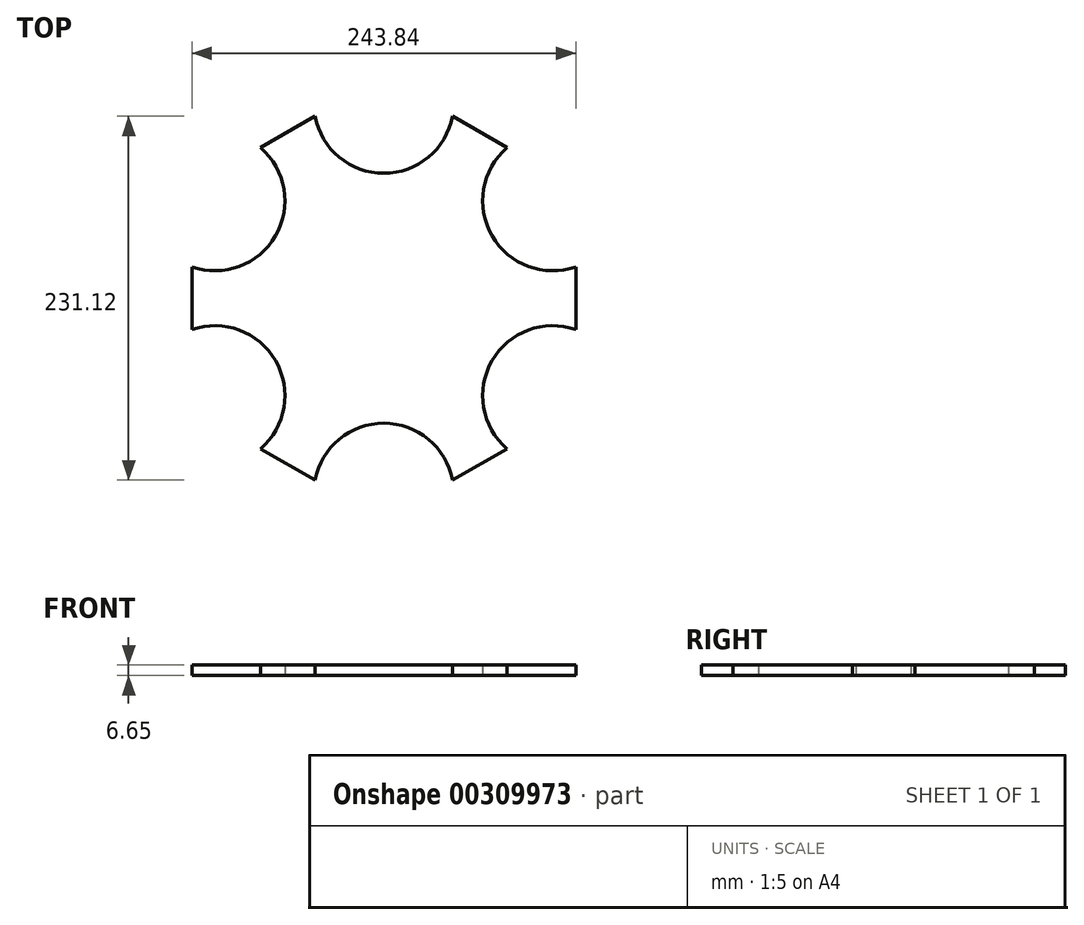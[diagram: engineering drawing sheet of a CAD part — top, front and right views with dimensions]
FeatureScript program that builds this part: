
annotation { "Feature Type Name" : "Feature", "Feature Type Description" : "" }
export const myFeature = defineFeature(function(context is Context, id is Id, definition is map)
    precondition{}
    {
        {
            var Q0;
            Q0=qCreatedBy(makeId("Top.planeOp"),FACE);
            var sketch = newSketch(context, id + "F0", { "sketchPlane" : qUnion([Q0])});
            skArc(sketch, "E0", {"start": v(-43.68, 115.56) * mm, "mid": v(0, 79.38) * mm, "end": v(43.68, 115.56) * mm});
            skArc(sketch, "E1.1.0", {"start": v(-121.92, 19.96) * mm, "mid": v(-68.74, 39.69) * mm, "end": v(-78.24, 95.6) * mm});
            skArc(sketch, "E1.2.0", {"start": v(-78.24, -95.6) * mm, "mid": v(-68.74, -39.69) * mm, "end": v(-121.92, -19.96) * mm});
            skArc(sketch, "E1.3.0", {"start": v(43.68, -115.56) * mm, "mid": v(0, -79.38) * mm, "end": v(-43.68, -115.56) * mm});
            skArc(sketch, "E1.4.0", {"start": v(121.92, -19.96) * mm, "mid": v(68.74, -39.69) * mm, "end": v(78.24, -95.6) * mm});
            skArc(sketch, "E1.5.0", {"start": v(78.24, 95.6) * mm, "mid": v(68.74, 39.69) * mm, "end": v(121.92, 19.96) * mm});
            skPoint(sketch, "E1.center", {"position": v(0, 0) * mm});
            skArc(sketch, "E2.cCircle", {"start": v(-137.66, 29.5) * mm, "mid": v(121.92, -70.4) * mm, "end": v(-94.38, 104.46) * mm, "construction": true});
            skLineSegment(sketch, "E2.0", {"start": v(43.68, 115.56) * mm, "end": v(78.24, 95.6) * mm});
            skLineSegment(sketch, "E2.1", {"start": v(121.92, 19.96) * mm, "end": v(121.92, -19.96) * mm});
            skLineSegment(sketch, "E2.2", {"start": v(78.24, -95.6) * mm, "end": v(43.68, -115.56) * mm});
            skLineSegment(sketch, "E2.3", {"start": v(-43.68, -115.56) * mm, "end": v(-78.24, -95.6) * mm});
            skLineSegment(sketch, "E2.4", {"start": v(-121.92, -19.96) * mm, "end": v(-121.92, 19.96) * mm});
            skLineSegment(sketch, "E2.5", {"start": v(-78.24, 95.6) * mm, "end": v(-43.68, 115.56) * mm});
            skPoint(sketch, "E3.orphan", {"position": v(-121.92, 70.4) * mm});
            skPoint(sketch, "E4.orphan", {"position": v(0, 140.78) * mm});
            skPoint(sketch, "E5.orphan", {"position": v(121.92, 70.4) * mm});
            skPoint(sketch, "E6.orphan", {"position": v(121.92, -70.4) * mm});
            skPoint(sketch, "E7.orphan", {"position": v(0, -140.78) * mm});
            skPoint(sketch, "E8.orphan", {"position": v(-121.92, -70.4) * mm});
            skSolve(sketch);
        }
        {
            var Q0;
            Q0 = qSketchRegion(id + "F0", true);
            extrude(context, id + "F1", {"entities" : qUnion([Q0]), "depth" : 6.65 * mm});
        }
    });
